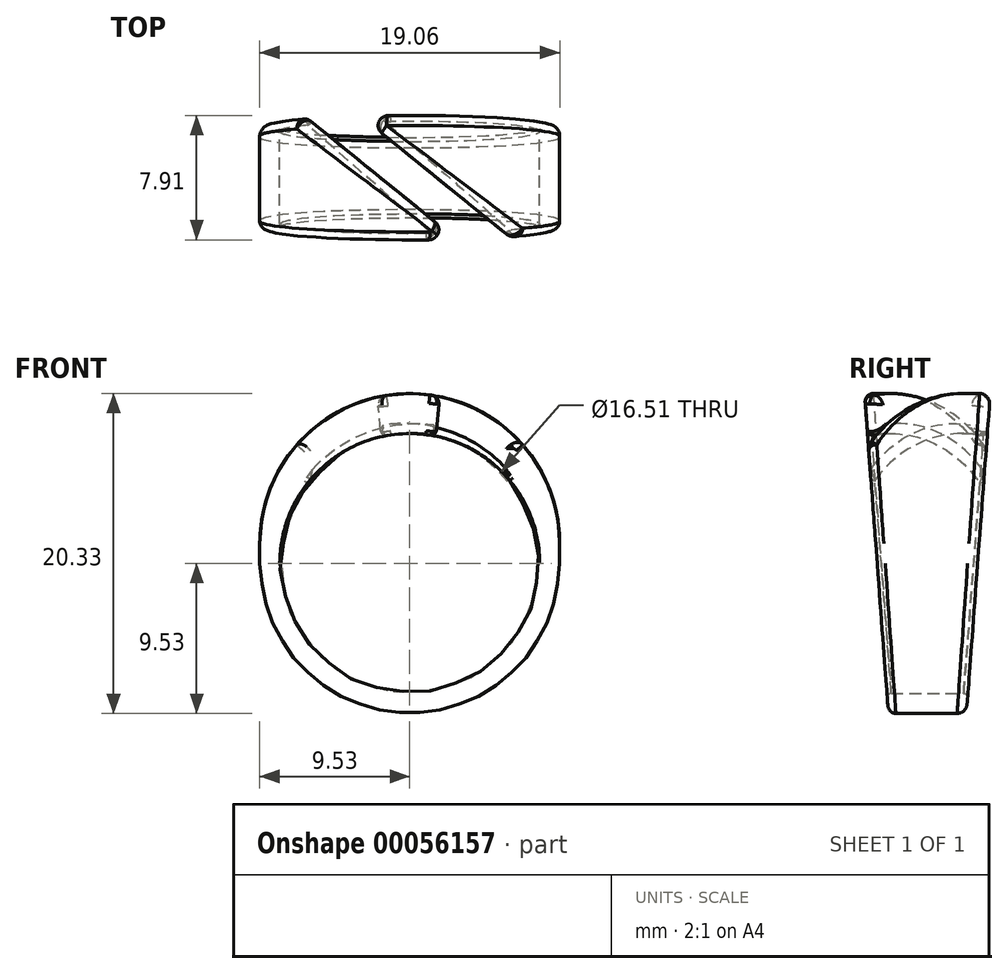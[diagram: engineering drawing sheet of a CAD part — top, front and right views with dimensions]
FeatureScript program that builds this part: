
annotation { "Feature Type Name" : "Feature", "Feature Type Description" : "" }
export const myFeature = defineFeature(function(context is Context, id is Id, definition is map)
    precondition{}
    {
        {
            var Q0;
            Q0=qCreatedBy(makeId("Front.planeOp"),FACE);
            var sketch = newSketch(context, id + "F0", { "sketchPlane" : qUnion([Q0])});
            skCircle(sketch, "E0", {"center": v(0, 0) * mm, "radius": 8.26 * mm});
            skArc(sketch, "E1", {"start": v(-9.53, 0) * mm, "mid": v(0, -9.53) * mm, "end": v(9.53, 0) * mm});
            skLineSegment(sketch, "E2", {"start": v(-9.53, 0) * mm, "end": v(-9.53, 1.27) * mm});
            skLineSegment(sketch, "E3", {"start": v(9.53, 0) * mm, "end": v(9.53, 1.27) * mm});
            skLineSegment(sketch, "E4", {"start": v(-9.53, 1.27) * mm, "end": v(9.53, 1.27) * mm, "construction": true});
            skPoint(sketch, "E5", {"position": v(0, 1.27) * mm});
            skArc(sketch, "E6", {"start": v(-9.53, 1.27) * mm, "mid": v(0, 10.8) * mm, "end": v(9.53, 1.27) * mm});
            skPoint(sketch, "E7", {"position": v(0, 8.26) * mm});
            skPoint(sketch, "E8", {"position": v(0, 10.8) * mm});
            skPoint(sketch, "E9", {"position": v(0, -8.26) * mm});
            skPoint(sketch, "E10", {"position": v(0, -9.53) * mm});
            skSolve(sketch);
        }
        {
            var Q0;
            Q0=qCreatedBy(makeId("Right.planeOp"),FACE);
            var sketch = newSketch(context, id + "F1", { "sketchPlane" : qUnion([Q0])});
            skLineSegment(sketch, "E11", {"start": v(-0.38, 4.06) * mm, "end": v(-0.38, -4.44) * mm, "construction": true});
            skLineSegment(sketch, "E12", {"start": v(0, 3.48) * mm, "end": v(-0.38, 3.48) * mm, "construction": true});
            skSolve(sketch);
        }
        {
            var Q0;
            Q0=makeQuery(id+"F0.imprint","IMPRINT",FACE,{"disambiguationData":[TD([[makeQuery(id+"F0.imprint","IMPRINT",EDGE,{"derivedFrom":sQuery(id+"F0.wireOp",EDGE,"E0")}),-1.0]])]});
            var Q1;
            Q1 = qSketchRegion(id + "F1", true);
            extrude(context, id + "F2", {"entities" : qUnion([Q0, Q1]), "depth" : 8 * mm});
        }
        {
            var Q0;
            Q0=qCreatedBy(makeId("Right.planeOp"),FACE);
            var sketch = newSketch(context, id + "F3", { "sketchPlane" : qUnion([Q0])});
            skLineSegment(sketch, "E13", {"start": v(0, 10.84) * mm, "end": v(-1.56, -9.94) * mm});
            skLineSegment(sketch, "E14", {"start": v(-1.56, -9.94) * mm, "end": v(0.84, -9.94) * mm});
            skLineSegment(sketch, "E15", {"start": v(0.84, -9.94) * mm, "end": v(1.17, 11.15) * mm});
            skLineSegment(sketch, "E16", {"start": v(1.17, 11.15) * mm, "end": v(0, 10.84) * mm});
            skLineSegment(sketch, "E17", {"start": v(-4, 1.27) * mm, "end": v(-4, 12.38) * mm, "construction": true});
            skLineSegment(sketch, "E18.MirrorCS", {"start": v(-6.44, -9.94) * mm, "end": v(-8.84, -9.94) * mm});
            skLineSegment(sketch, "E19.MirrorCS", {"start": v(-9.17, 11.15) * mm, "end": v(-8, 10.84) * mm});
            skLineSegment(sketch, "E20.MirrorCS", {"start": v(-8.84, -9.94) * mm, "end": v(-9.17, 11.15) * mm});
            skLineSegment(sketch, "E21.MirrorCS", {"start": v(-8, 10.84) * mm, "end": v(-6.44, -9.94) * mm});
            skSolve(sketch);
        }
        {
            var Q0;
            Q0 = qSketchRegion(id + "F3", true);
            extrude(context, id + "F4", {"entities" : qUnion([Q0]), "operationType" : NewBodyOperationType.REMOVE, "endBound" : BoundingType.THROUGH_ALL, "depth" : 25.4 * mm, "hasSecondDirection" : true, "secondDirectionBound" : SecondDirectionBoundingType.THROUGH_ALL, "secondDirectionOppositeDirection" : true, "secondDirectionDepth" : 25.4 * mm});
        }
        {
            var Q0;
            Q0=makeQuery(id+"F4.boolean.opBoolean","INTERSECT",EDGE,{"derivedFrom":[makeQuery(id+"F2.opExtrude","SWEPT_FACE",FACE,{"disambiguationData":[OSD([sQuery(id+"F0.wireOp",EDGE,"E0")])]}),makeQuery(id+"F4.opExtrude","SWEPT_FACE",FACE,{"disambiguationData":[OSD([sQuery(id+"F3.wireOp",EDGE,"E21.MirrorCS")])]})]});
            var Q1;
            Q1=makeQuery(id+"F4.boolean.opBoolean","INTERSECT",EDGE,{"derivedFrom":[makeQuery(id+"F2.opExtrude","SWEPT_FACE",FACE,{"disambiguationData":[OSD([sQuery(id+"F0.wireOp",EDGE,"E0")])]}),makeQuery(id+"F4.opExtrude","SWEPT_FACE",FACE,{"disambiguationData":[OSD([sQuery(id+"F3.wireOp",EDGE,"E13")])]})]});
            fillet(context, id + "F5", {"entities" : qUnion([Q0, Q1]), "radius" : 0.25 * mm, "tangentPropagation" : true, "allowEdgeOverflow" : false});
        }
        {
            var Q0;
            Q0=makeQuery(id+"F4.boolean.opBoolean","INTERSECT",EDGE,{"derivedFrom":[makeQuery(id+"F2.opExtrude","SWEPT_FACE",FACE,{"disambiguationData":[OSD([sQuery(id+"F0.wireOp",EDGE,"E1")])]}),makeQuery(id+"F4.opExtrude","SWEPT_FACE",FACE,{"disambiguationData":[OSD([sQuery(id+"F3.wireOp",EDGE,"E21.MirrorCS")])]})]});
            var Q1;
            Q1=makeQuery(id+"F4.boolean.opBoolean","INTERSECT",EDGE,{"derivedFrom":[makeQuery(id+"F2.opExtrude","SWEPT_FACE",FACE,{"disambiguationData":[OSD([sQuery(id+"F0.wireOp",EDGE,"E3")])]}),makeQuery(id+"F4.opExtrude","SWEPT_FACE",FACE,{"disambiguationData":[OSD([sQuery(id+"F3.wireOp",EDGE,"E21.MirrorCS")])]})]});
            var Q2;
            Q2=makeQuery(id+"F4.boolean.opBoolean","INTERSECT",EDGE,{"derivedFrom":[makeQuery(id+"F2.opExtrude","SWEPT_FACE",FACE,{"disambiguationData":[OSD([sQuery(id+"F0.wireOp",EDGE,"E6")])]}),makeQuery(id+"F4.opExtrude","SWEPT_FACE",FACE,{"disambiguationData":[OSD([sQuery(id+"F3.wireOp",EDGE,"E21.MirrorCS")])]})]});
            var Q3;
            Q3=makeQuery(id+"F4.boolean.opBoolean","INTERSECT",EDGE,{"derivedFrom":[makeQuery(id+"F2.opExtrude","SWEPT_FACE",FACE,{"disambiguationData":[OSD([sQuery(id+"F0.wireOp",EDGE,"E2")])]}),makeQuery(id+"F4.opExtrude","SWEPT_FACE",FACE,{"disambiguationData":[OSD([sQuery(id+"F3.wireOp",EDGE,"E21.MirrorCS")])]})]});
            fillet(context, id + "F6", {"entities" : qUnion([Q0, Q1, Q2, Q3]), "radius" : 0.5 * mm, "tangentPropagation" : true, "allowEdgeOverflow" : false});
        }
        {
            var Q0;
            Q0=makeQuery(id+"F4.boolean.opBoolean","INTERSECT",EDGE,{"derivedFrom":[makeQuery(id+"F2.opExtrude","SWEPT_FACE",FACE,{"disambiguationData":[OSD([sQuery(id+"F0.wireOp",EDGE,"E6")])]}),makeQuery(id+"F4.opExtrude","SWEPT_FACE",FACE,{"disambiguationData":[OSD([sQuery(id+"F3.wireOp",EDGE,"E13")])]})]});
            var Q1;
            Q1=makeQuery(id+"F4.boolean.opBoolean","INTERSECT",EDGE,{"derivedFrom":[makeQuery(id+"F2.opExtrude","SWEPT_FACE",FACE,{"disambiguationData":[OSD([sQuery(id+"F0.wireOp",EDGE,"E3")])]}),makeQuery(id+"F4.opExtrude","SWEPT_FACE",FACE,{"disambiguationData":[OSD([sQuery(id+"F3.wireOp",EDGE,"E13")])]})]});
            var Q2;
            Q2=makeQuery(id+"F4.boolean.opBoolean","INTERSECT",EDGE,{"derivedFrom":[makeQuery(id+"F2.opExtrude","SWEPT_FACE",FACE,{"disambiguationData":[OSD([sQuery(id+"F0.wireOp",EDGE,"E1")])]}),makeQuery(id+"F4.opExtrude","SWEPT_FACE",FACE,{"disambiguationData":[OSD([sQuery(id+"F3.wireOp",EDGE,"E13")])]})]});
            var Q3;
            Q3=makeQuery(id+"F4.boolean.opBoolean","INTERSECT",EDGE,{"derivedFrom":[makeQuery(id+"F2.opExtrude","SWEPT_FACE",FACE,{"disambiguationData":[OSD([sQuery(id+"F0.wireOp",EDGE,"E2")])]}),makeQuery(id+"F4.opExtrude","SWEPT_FACE",FACE,{"disambiguationData":[OSD([sQuery(id+"F3.wireOp",EDGE,"E13")])]})]});
            fillet(context, id + "F7", {"entities" : qUnion([Q0, Q1, Q2, Q3]), "radius" : 0.64 * mm, "tangentPropagation" : true, "allowEdgeOverflow" : false});
        }
        {
            var Q0;
            Q0=qCreatedBy(makeId("Top.planeOp"),FACE);
            var sketch = newSketch(context, id + "F8", { "sketchPlane" : qUnion([Q0])});
            skLineSegment(sketch, "E22", {"start": v(-7.56, 0.61) * mm, "end": v(5.52, -9.99) * mm});
            skLineSegment(sketch, "E23", {"start": v(5.52, -9.99) * mm, "end": v(7.1, -8.38) * mm});
            skLineSegment(sketch, "E24", {"start": v(7.1, -8.38) * mm, "end": v(-6.06, 2.29) * mm});
            skLineSegment(sketch, "E25", {"start": v(-6.06, 2.29) * mm, "end": v(-7.56, 0.61) * mm});
            skLineSegment(sketch, "E26", {"start": v(-5.79, -0.82) * mm, "end": v(-5.79, 4.85) * mm, "construction": true});
            skLineSegment(sketch, "E27", {"start": v(-5.79, -0.82) * mm, "end": v(-9.53, -0.82) * mm, "construction": true});
            skLineSegment(sketch, "E28", {"start": v(5.79, -7.31) * mm, "end": v(9.52, -7.31) * mm, "construction": true});
            skLineSegment(sketch, "E29", {"start": v(5.79, -7.31) * mm, "end": v(5.79, -12.98) * mm, "construction": true});
            skSolve(sketch);
        }
        {
            var Q0;
            Q0=makeQuery(id+"F8.imprint","IMPRINT",FACE,{"disambiguationData":[TD([[makeQuery(id+"F8.imprint","IMPRINT",EDGE,{"derivedFrom":sQuery(id+"F8.wireOp",EDGE,"E22")}),1.0]])]});
            extrude(context, id + "F9", {"entities" : qUnion([Q0]), "operationType" : NewBodyOperationType.REMOVE, "depth" : 25.4 * mm});
        }
        {
            var Q0;
            Q0=makeQuery(id+"F9.boolean.opBoolean","INTERSECT",EDGE,{"derivedFrom":[makeQuery(id+"F4.boolean.opBoolean","COPY",FACE,{"derivedFrom":makeQuery(id+"F4.opExtrude","SWEPT_FACE",FACE,{"disambiguationData":[OSD([sQuery(id+"F3.wireOp",EDGE,"E21.MirrorCS")])]})}),makeQuery(id+"F9.opExtrude","SWEPT_FACE",FACE,{"disambiguationData":[OSD([sQuery(id+"F8.wireOp",EDGE,"E24")])]})]});
            var Q1;
            Q1=makeQuery(id+"F9.boolean.opBoolean","INTERSECT",EDGE,{"derivedFrom":[makeQuery(id+"F4.boolean.opBoolean","COPY",FACE,{"derivedFrom":makeQuery(id+"F4.opExtrude","SWEPT_FACE",FACE,{"disambiguationData":[OSD([sQuery(id+"F3.wireOp",EDGE,"E21.MirrorCS")])]})}),makeQuery(id+"F9.opExtrude","SWEPT_FACE",FACE,{"disambiguationData":[OSD([sQuery(id+"F8.wireOp",EDGE,"E22")])]})]});
            var Q2;
            Q2=makeQuery(id+"F9.boolean.opBoolean","INTERSECT",EDGE,{"derivedFrom":[makeQuery(id+"F4.boolean.opBoolean","COPY",FACE,{"derivedFrom":makeQuery(id+"F4.opExtrude","SWEPT_FACE",FACE,{"disambiguationData":[OSD([sQuery(id+"F3.wireOp",EDGE,"E13")])]})}),makeQuery(id+"F9.opExtrude","SWEPT_FACE",FACE,{"disambiguationData":[OSD([sQuery(id+"F8.wireOp",EDGE,"E24")])]})]});
            var Q3;
            Q3=makeQuery(id+"F9.boolean.opBoolean","INTERSECT",EDGE,{"derivedFrom":[makeQuery(id+"F4.boolean.opBoolean","COPY",FACE,{"derivedFrom":makeQuery(id+"F4.opExtrude","SWEPT_FACE",FACE,{"disambiguationData":[OSD([sQuery(id+"F3.wireOp",EDGE,"E13")])]})}),makeQuery(id+"F9.opExtrude","SWEPT_FACE",FACE,{"disambiguationData":[OSD([sQuery(id+"F8.wireOp",EDGE,"E22")])]})]});
            fillet(context, id + "F10", {"entities" : qUnion([Q0, Q1, Q2, Q3]), "radius" : 0.64 * mm, "tangentPropagation" : true, "allowEdgeOverflow" : false});
        }
    });
